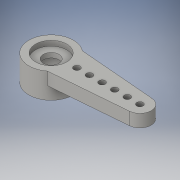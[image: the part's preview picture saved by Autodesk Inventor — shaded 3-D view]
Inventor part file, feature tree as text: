
AUTODESK INVENTOR PART (.ipt)
format: ipt  version: 2016 (Build 200138000, 138)  size: 162,304 bytes
history: native  units: in
note: dims shown in document units (in); Inventor stores cm internally (conversion verified against a paired STEP export)
features: other x3, sketch x1
ambient origin geometry x8: Origin, YZ Plane, XZ Plane, XY Plane, X Axis, Y Axis, Z Axis, Center Point
bodies: Solid1 (feature_tree)
feature tree (4):
  other  "SG90 plastic Horn.ipt"
  other  "Solid1::SG90 plastic Horn.ipt"
  other  "TaggingFeature1"
  sketch  "Sketch1"  dims[d0=0.3937in]
